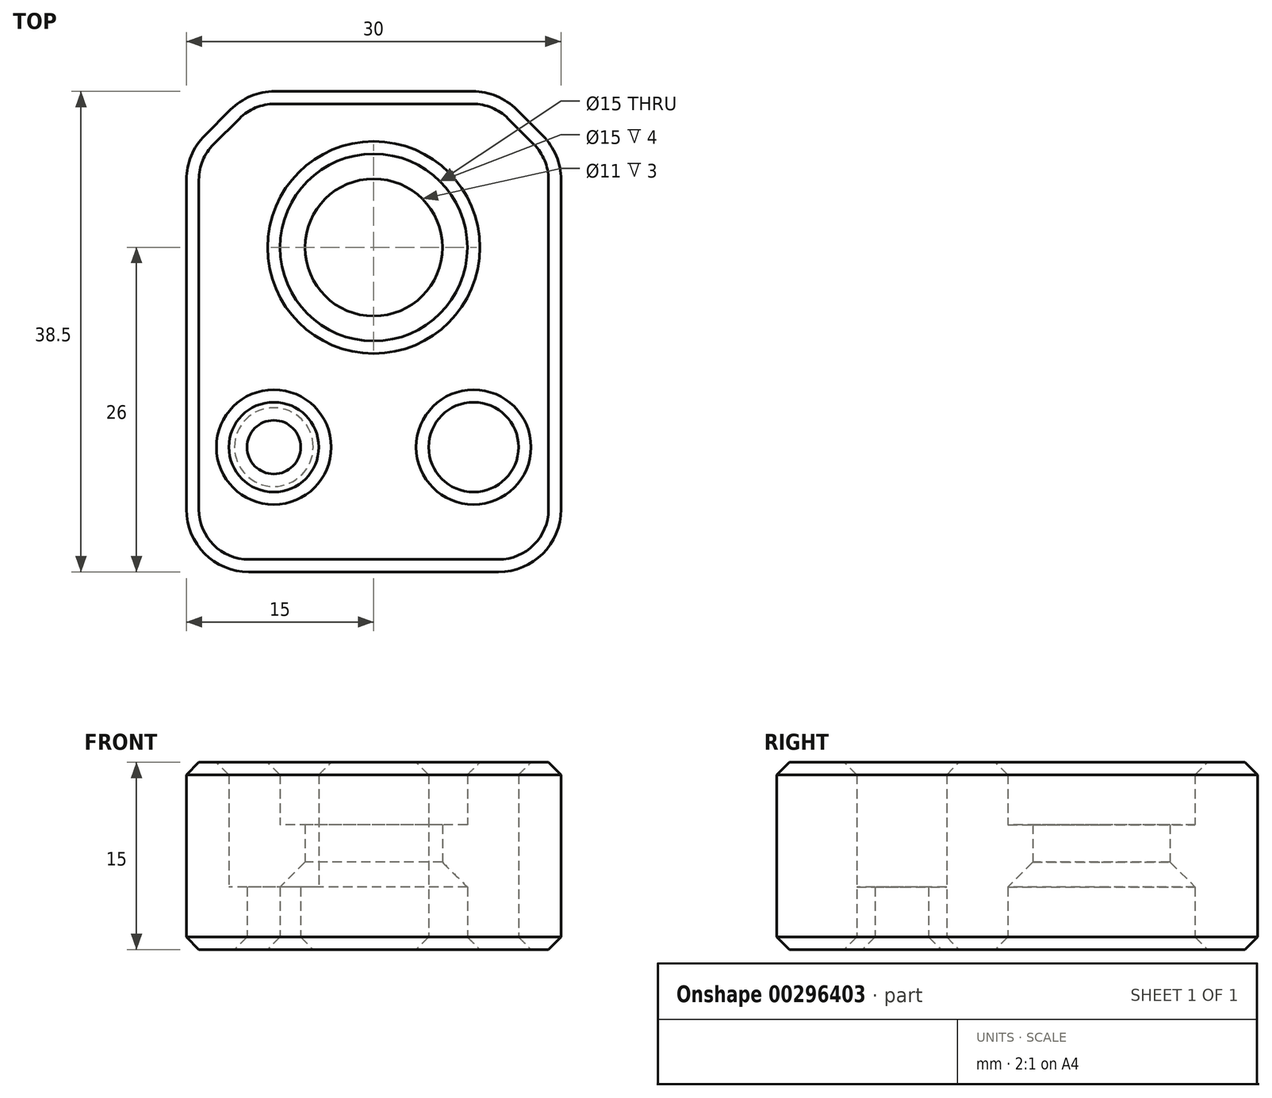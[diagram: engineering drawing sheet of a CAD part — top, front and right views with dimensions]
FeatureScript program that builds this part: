
annotation { "Feature Type Name" : "Feature", "Feature Type Description" : "" }
export const myFeature = defineFeature(function(context is Context, id is Id, definition is map)
    precondition{}
    {
        {
            var Q0;
            Q0=qCreatedBy(makeId("Top.planeOp"),FACE);
            var sketch = newSketch(context, id + "F0", { "sketchPlane" : qUnion([Q0])});
            skLineSegment(sketch, "E0.bottom", {"start": v(15, -19.25) * mm, "end": v(-15, -19.25) * mm});
            skLineSegment(sketch, "E0.top", {"start": v(15, 19.25) * mm, "end": v(-15, 19.25) * mm});
            skLineSegment(sketch, "E0.left", {"start": v(15, -19.25) * mm, "end": v(15, 19.25) * mm});
            skLineSegment(sketch, "E0.right", {"start": v(-15, -19.25) * mm, "end": v(-15, 19.25) * mm});
            skPoint(sketch, "E0.middle", {"position": v(0, 0) * mm});
            skLineSegment(sketch, "E1", {"start": v(-15, 0.75) * mm, "end": v(15, 0.75) * mm, "construction": true});
            skLineSegment(sketch, "E2", {"start": v(-15, -9.25) * mm, "end": v(15, -9.25) * mm, "construction": true});
            skCircle(sketch, "E3", {"center": v(0, 6.75) * mm, "radius": 7.5 * mm});
            skCircle(sketch, "E4", {"center": v(0, 6.75) * mm, "radius": 5.5 * mm});
            skCircle(sketch, "E5", {"center": v(0, 6.75) * mm, "radius": 3 * mm, "construction": true});
            skCircle(sketch, "E6", {"center": v(-8, -9.25) * mm, "radius": 2.15 * mm});
            skCircle(sketch, "E7", {"center": v(-8, -9.25) * mm, "radius": 3.6 * mm});
            skCircle(sketch, "E8.MirrorC", {"center": v(8, -9.25) * mm, "radius": 3.6 * mm});
            skCircle(sketch, "E9.MirrorC", {"center": v(8, -9.25) * mm, "radius": 2.15 * mm});
            skSolve(sketch);
        }
        {
            var Q0;
            Q0=makeQuery(id+"F0.imprint","IMPRINT",FACE,{"disambiguationData":[TD([[makeQuery(id+"F0.imprint","IMPRINT",EDGE,{"derivedFrom":sQuery(id+"F0.wireOp",EDGE,"E0.bottom")}),-1.0]])]});
            extrude(context, id + "F1", {"entities" : qUnion([Q0]), "depth" : 15 * mm, "offsetDistance" : 25 * mm});
        }
        {
            var Q0;
            Q0=makeQuery(id+"F0.imprint","IMPRINT",FACE,{"disambiguationData":[TD([[makeQuery(id+"F0.imprint","IMPRINT",EDGE,{"derivedFrom":sQuery(id+"F0.wireOp",EDGE,"E6")}),-1.0]])]});
            var Q1;
            Q1=makeQuery(id+"F0.imprint","IMPRINT",FACE,{"disambiguationData":[TD([[makeQuery(id+"F0.imprint","IMPRINT",EDGE,{"derivedFrom":sQuery(id+"F0.wireOp",EDGE,"E8.MirrorC")}),-1.0]])]});
            extrude(context, id + "F2", {"entities" : qUnion([Q0, Q1]), "operationType" : NewBodyOperationType.ADD, "depth" : 5 * mm, "offsetDistance" : 25 * mm});
        }
        {
            var Q0;
            Q0=makeQuery(id+"F0.imprint","IMPRINT",FACE,{"disambiguationData":[TD([[makeQuery(id+"F0.imprint","IMPRINT",EDGE,{"derivedFrom":sQuery(id+"F0.wireOp",EDGE,"E3")}),1.0]])]});
            extrude(context, id + "F3", {"entities" : qUnion([Q0]), "operationType" : NewBodyOperationType.ADD, "depth" : (15 - 5) * mm, "offsetDistance" : 25 * mm, "hasSecondDirection" : true, "secondDirectionOppositeDirection" : false, "secondDirectionDepth" : 5 * mm});
        }
        {
            var Q0;
            Q0=makeQuery(id+"F3.opExtrude","CAP_EDGE",EDGE,{"disambiguationData":[OSD([sQuery(id+"F0.wireOp",EDGE,"E4")])],"isStart":true});
            chamfer(context, id + "F4", {"entities" : qUnion([Q0]), "width" : 2 * mm, "tangentPropagation" : true});
        }
        {
            var Q0;
            Q0=makeQuery(id+"F1.opExtrude","SWEPT_EDGE",EDGE,{"disambiguationData":[OSD([sQuery(id+"F0.wireOp",EDGE,"E0.top"),sQuery(id+"F0.wireOp",EDGE,"E0.left")])]});
            var Q1;
            Q1=makeQuery(id+"F1.opExtrude","SWEPT_EDGE",EDGE,{"disambiguationData":[OSD([sQuery(id+"F0.wireOp",EDGE,"E0.top"),sQuery(id+"F0.wireOp",EDGE,"E0.right")])]});
            chamfer(context, id + "F5", {"entities" : qUnion([Q0, Q1]), "width" : 5 * mm, "tangentPropagation" : true});
        }
        {
            var Q0;
            Q0=makeQuery(id+"F1.opExtrude","SWEPT_EDGE",EDGE,{"disambiguationData":[OSD([sQuery(id+"F0.wireOp",EDGE,"E0.bottom"),sQuery(id+"F0.wireOp",EDGE,"E0.left")])]});
            var Q1;
            Q1=makeQuery(id+"F1.opExtrude","SWEPT_EDGE",EDGE,{"disambiguationData":[OSD([sQuery(id+"F0.wireOp",EDGE,"E0.bottom"),sQuery(id+"F0.wireOp",EDGE,"E0.right")])]});
            fillet(context, id + "F6", {"entities" : qUnion([Q0, Q1]), "radius" : 5 * mm, "tangentPropagation" : true, "allowEdgeOverflow" : false});
        }
        {
            var Q0;
            {var subQ0=sQuery(id+"F0.wireOp",EDGE,"E0.left");Q0=makeQuery(id+"F5.opChamfer","BLEND_EDGE",EDGE,{"blendedFrom":[makeQuery(id+"F1.opExtrude","SWEPT_EDGE",EDGE,{"disambiguationData":[OSD([sQuery(id+"F0.wireOp",EDGE,"E0.top"),subQ0])]}),makeQuery(id+"F1.opExtrude","SWEPT_FACE",FACE,{"disambiguationData":[OSD([subQ0])]})],"blendedInto":[makeQuery(id+"F1.opExtrude","SWEPT_FACE",FACE,{"disambiguationData":[OSD([subQ0])]})]});}
            var Q1;
            {var subQ0=sQuery(id+"F0.wireOp",EDGE,"E0.top");Q1=makeQuery(id+"F5.opChamfer","BLEND_EDGE",EDGE,{"blendedFrom":[makeQuery(id+"F1.opExtrude","SWEPT_EDGE",EDGE,{"disambiguationData":[OSD([subQ0,sQuery(id+"F0.wireOp",EDGE,"E0.left")])]}),makeQuery(id+"F1.opExtrude","SWEPT_FACE",FACE,{"disambiguationData":[OSD([subQ0])]})],"blendedInto":[makeQuery(id+"F1.opExtrude","SWEPT_FACE",FACE,{"disambiguationData":[OSD([subQ0])]})]});}
            var Q2;
            {var subQ0=sQuery(id+"F0.wireOp",EDGE,"E0.top");Q2=makeQuery(id+"F5.opChamfer","BLEND_EDGE",EDGE,{"blendedFrom":[makeQuery(id+"F1.opExtrude","SWEPT_EDGE",EDGE,{"disambiguationData":[OSD([subQ0,sQuery(id+"F0.wireOp",EDGE,"E0.right")])]}),makeQuery(id+"F1.opExtrude","SWEPT_FACE",FACE,{"disambiguationData":[OSD([subQ0])]})],"blendedInto":[makeQuery(id+"F1.opExtrude","SWEPT_FACE",FACE,{"disambiguationData":[OSD([subQ0])]})]});}
            var Q3;
            {var subQ0=sQuery(id+"F0.wireOp",EDGE,"E0.right");Q3=makeQuery(id+"F5.opChamfer","BLEND_EDGE",EDGE,{"blendedFrom":[makeQuery(id+"F1.opExtrude","SWEPT_EDGE",EDGE,{"disambiguationData":[OSD([sQuery(id+"F0.wireOp",EDGE,"E0.top"),subQ0])]}),makeQuery(id+"F1.opExtrude","SWEPT_FACE",FACE,{"disambiguationData":[OSD([subQ0])]})],"blendedInto":[makeQuery(id+"F1.opExtrude","SWEPT_FACE",FACE,{"disambiguationData":[OSD([subQ0])]})]});}
            fillet(context, id + "F7", {"entities" : qUnion([Q0, Q1, Q2, Q3]), "radius" : 5 * mm, "tangentPropagation" : true, "allowEdgeOverflow" : false});
        }
        {
            var Q0;
            Q0=makeQuery(id+"F1.opExtrude","CAP_FACE",FACE,{"disambiguationData":[OSD([sQuery(id+"F0.wireOp",EDGE,"E0.bottom"),sQuery(id+"F0.wireOp",EDGE,"E0.top"),sQuery(id+"F0.wireOp",EDGE,"E0.left"),sQuery(id+"F0.wireOp",EDGE,"E0.right"),sQuery(id+"F0.wireOp",EDGE,"E3"),sQuery(id+"F0.wireOp",EDGE,"E7"),sQuery(id+"F0.wireOp",EDGE,"E8.MirrorC")])],"isStart":false});
            var Q1;
            {var subQ0=sQuery(id+"F0.wireOp",EDGE,"E8.MirrorC");var subQ1=sQuery(id+"F0.wireOp",EDGE,"E7");Q1=makeQuery(id+"F2.boolean.opBoolean","MERGE",FACE,{"derivedFrom":[makeQuery(id+"F1.opExtrude","CAP_FACE",FACE,{"disambiguationData":[OSD([sQuery(id+"F0.wireOp",EDGE,"E0.bottom"),sQuery(id+"F0.wireOp",EDGE,"E0.top"),sQuery(id+"F0.wireOp",EDGE,"E0.left"),sQuery(id+"F0.wireOp",EDGE,"E0.right"),sQuery(id+"F0.wireOp",EDGE,"E3"),subQ1,subQ0])],"isStart":true}),makeQuery(id+"F2.opExtrude","CAP_FACE",FACE,{"disambiguationData":[OSD([sQuery(id+"F0.wireOp",EDGE,"E6"),subQ1])],"isStart":true}),makeQuery(id+"F2.opExtrude","CAP_FACE",FACE,{"disambiguationData":[OSD([subQ0,sQuery(id+"F0.wireOp",EDGE,"E9.MirrorC")])],"isStart":true})]});}
            chamfer(context, id + "F8", {"entities" : qUnion([Q0, Q1]), "width" : 1 * mm, "tangentPropagation" : true});
        }
    });
